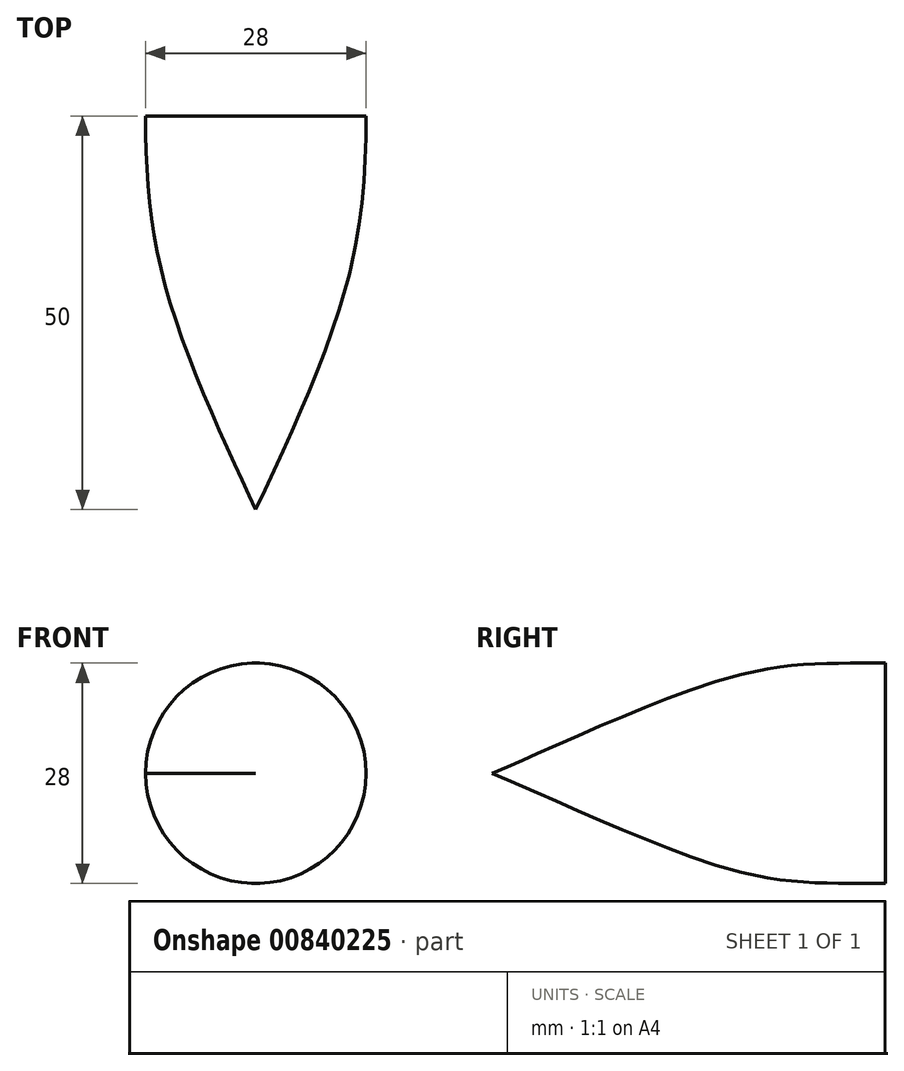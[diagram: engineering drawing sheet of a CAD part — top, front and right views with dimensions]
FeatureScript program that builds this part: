
annotation { "Feature Type Name" : "Feature", "Feature Type Description" : "" }
export const myFeature = defineFeature(function(context is Context, id is Id, definition is map)
    precondition{}
    {
        {
            var Q0;
            Q0=qCreatedBy(makeId("Front.planeOp"),FACE);
            var sketch = newSketch(context, id + "F0", { "sketchPlane" : qUnion([Q0])});
            skCircle(sketch, "E0", {"center": v(0, 0) * mm, "radius": 14 * mm});
            skLineSegment(sketch, "E1", {"start": v(-14, 0) * mm, "end": v(14, 0) * mm, "construction": true});
            skLineSegment(sketch, "E2", {"start": v(0, 14) * mm, "end": v(0, -14) * mm, "construction": true});
            skSolve(sketch);
        }
        {
            var Q0;
            Q0=qCreatedBy(makeId("Top.planeOp"),FACE);
            var sketch = newSketch(context, id + "F1", { "sketchPlane" : qUnion([Q0])});
            skLineSegment(sketch, "E3", {"start": v(0, 0) * mm, "end": v(0, -50) * mm, "construction": true});
            skFitSpline(sketch, "E4", {"points": [v(-14, 0) * mm, v(-10.85, -23.77) * mm, v(0, -50) * mm], "startDerivative": vector(0, -53.42) * mm, "endDerivative": vector(18.8, -39.9) * mm});
            skFitSpline(sketch, "E5.MirrorCS", {"points": [v(14, 0) * mm, v(10.85, -23.77) * mm, v(0, -50) * mm], "startDerivative": vector(0, -53.42) * mm, "endDerivative": vector(-18.8, -39.9) * mm});
            skSolve(sketch);
        }
        {
            var Q0;
            Q0=qCreatedBy(makeId("Right.planeOp"),FACE);
            var sketch = newSketch(context, id + "F2", { "sketchPlane" : qUnion([Q0])});
            skFitSpline(sketch, "E6", {"points": [v(0, 14) * mm, v(-21.08, 11.81) * mm, v(-50, 0) * mm], "startDerivative": vector(-58.46, 0) * mm, "endDerivative": vector(-35.67, -14.75) * mm});
            skFitSpline(sketch, "E7.MirrorCS", {"points": [v(0, -14) * mm, v(-21.08, -11.81) * mm, v(-50, 0) * mm], "startDerivative": vector(-58.46, 0) * mm, "endDerivative": vector(-35.67, 14.75) * mm});
            skSolve(sketch);
        }
        {
            var Q0;
            Q0=makeQuery(id+"F0.imprint","IMPRINT",FACE,{"disambiguationData":[TD([[makeQuery(id+"F0.imprint","IMPRINT",EDGE,{"derivedFrom":sQuery(id+"F0.wireOp",EDGE,"E0")}),1.0]])]});
            var Q1;
            Q1=sQuery(id+"F1.wireOp",VERTEX,"E3.end");
            var Q2;
            Q2=sQuery(id+"F2.wireOp",EDGE,"E6");
            var Q3;
            Q3=sQuery(id+"F1.wireOp",EDGE,"E5.MirrorCS");
            var Q4;
            Q4=sQuery(id+"F1.wireOp",EDGE,"E4");
            var Q5;
            Q5=sQuery(id+"F2.wireOp",EDGE,"E7.MirrorCS");
            loft(context, id + "F3", {"addGuides" : true, "sheetProfilesArray" : [{ "sheetProfileEntities" : qUnion([Q0]) }, { "sheetProfileEntities" : qUnion([Q1]) }], "guidesArray" : [{ "guideEntities" : qUnion([Q2]), "guideDerivativeType" : LoftGuideDerivativeType.DEFAULT, "guideDerivativeMagnitude" : 1 }, { "guideEntities" : qUnion([Q3]), "guideDerivativeType" : LoftGuideDerivativeType.DEFAULT, "guideDerivativeMagnitude" : 1 }, { "guideEntities" : qUnion([Q4]), "guideDerivativeType" : LoftGuideDerivativeType.DEFAULT, "guideDerivativeMagnitude" : 1 }, { "guideEntities" : qUnion([Q5]), "guideDerivativeType" : LoftGuideDerivativeType.DEFAULT, "guideDerivativeMagnitude" : 1 }]});
        }
    });
